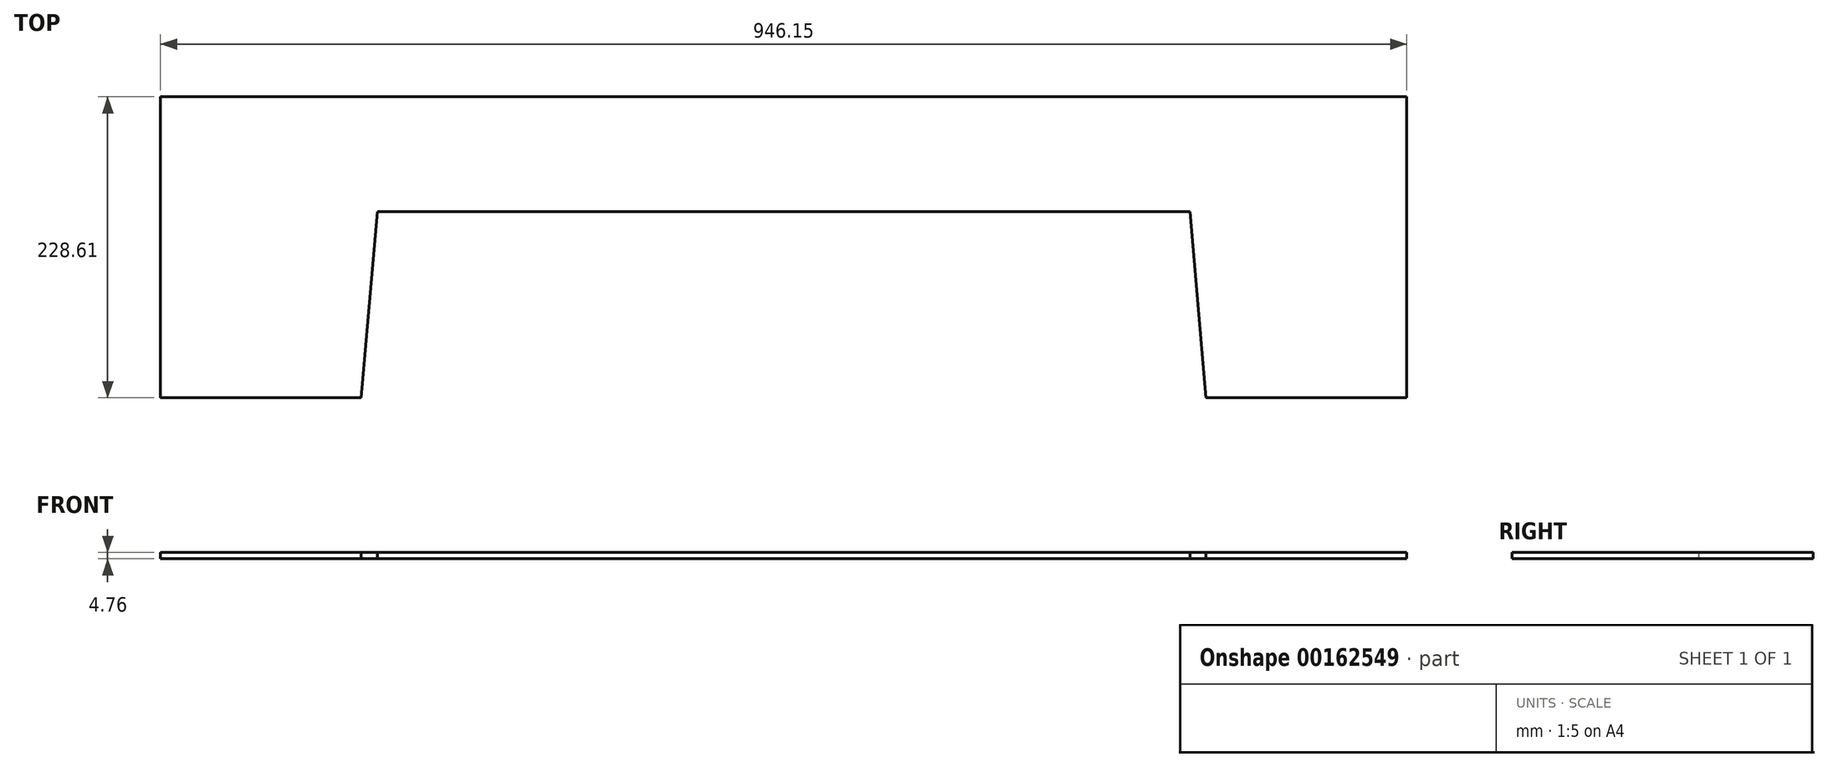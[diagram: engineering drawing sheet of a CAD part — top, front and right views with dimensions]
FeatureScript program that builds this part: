
annotation { "Feature Type Name" : "Feature", "Feature Type Description" : "" }
export const myFeature = defineFeature(function(context is Context, id is Id, definition is map)
    precondition{}
    {
        {
            var Q0;
            Q0=qCreatedBy(makeId("Top.planeOp"),FACE);
            var sketch = newSketch(context, id + "F0", { "sketchPlane" : qUnion([Q0])});
            skLineSegment(sketch, "E0.left", {"start": v(235.8, 115.25) * mm, "end": v(235.8, -113.35) * mm});
            skLineSegment(sketch, "E0.right", {"start": v(-710.36, 115.24) * mm, "end": v(-710.36, -113.36) * mm});
            skPoint(sketch, "E1.orphan", {"position": v(555.12, 48.59) * mm});
            skPoint(sketch, "E2.orphan", {"position": v(-557.96, -113.36) * mm});
            skLineSegment(sketch, "E3", {"start": v(-710.36, -113.36) * mm, "end": v(-557.96, -113.36) * mm});
            skLineSegment(sketch, "E4", {"start": v(83.4, -113.35) * mm, "end": v(235.8, -113.35) * mm});
            skLineSegment(sketch, "E5", {"start": v(-710.36, 115.24) * mm, "end": v(235.8, 115.25) * mm});
            skLineSegment(sketch, "E6.top", {"start": v(-545.73, 28.15) * mm, "end": v(71.15, 28.15) * mm});
            skLineSegment(sketch, "E7", {"start": v(-557.96, -113.36) * mm, "end": v(-545.73, 28.15) * mm});
            skLineSegment(sketch, "E8", {"start": v(83.4, -113.35) * mm, "end": v(71.15, 28.15) * mm});
            skSolve(sketch);
        }
        {
            var Q0;
            Q0=qSketchRegion(id+"F0",true);
            extrude(context, id + "F1", {"entities" : qUnion([Q0]), "depth" : 4.76 * mm});
        }
    });
